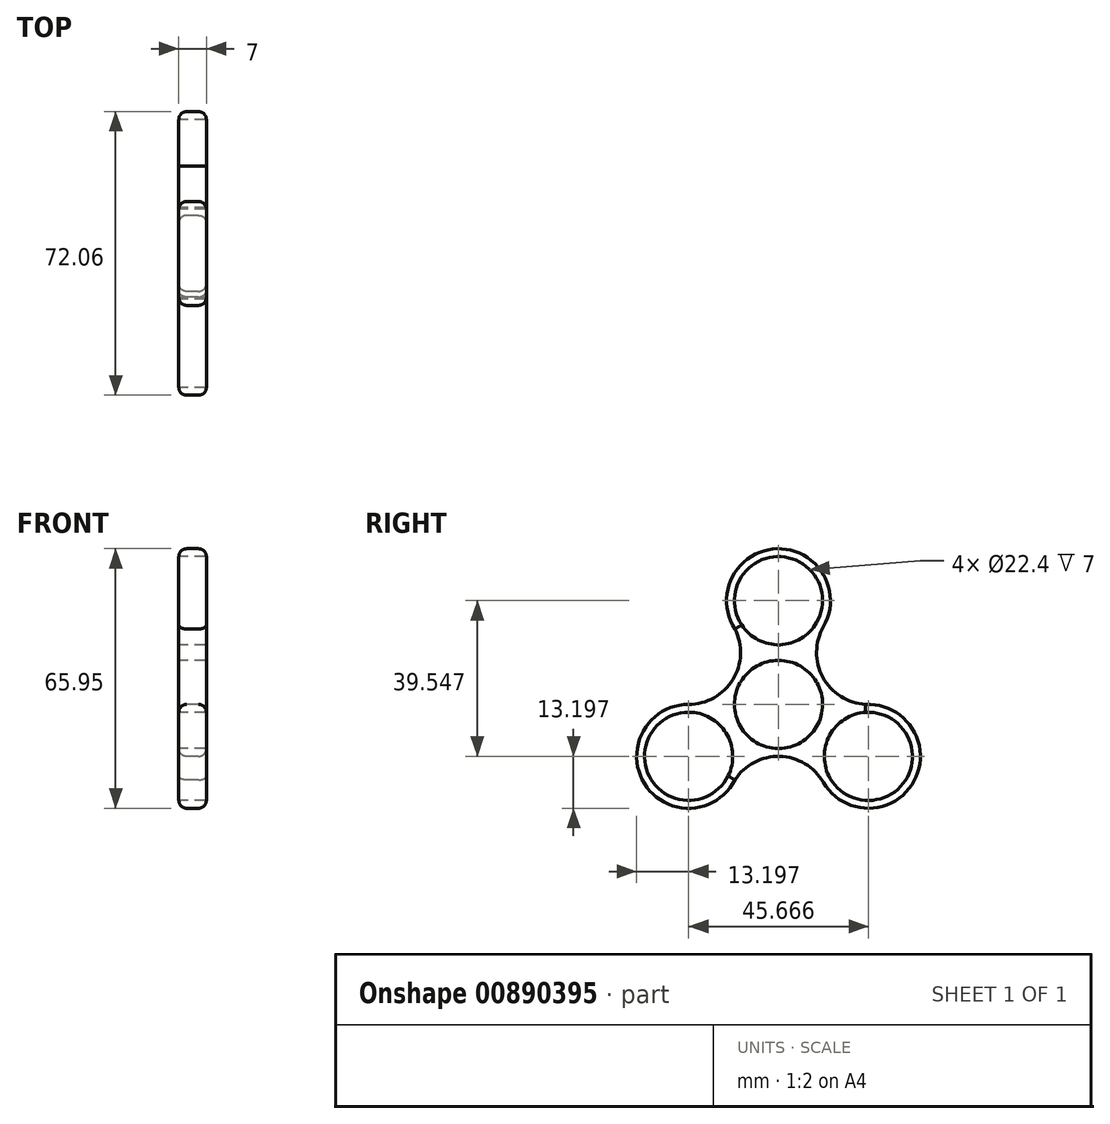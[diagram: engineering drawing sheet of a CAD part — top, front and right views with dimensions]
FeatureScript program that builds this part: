
annotation { "Feature Type Name" : "Feature", "Feature Type Description" : "" }
export const myFeature = defineFeature(function(context is Context, id is Id, definition is map)
    precondition{}
    {
        {
            var Q0;
            Q0=qCreatedBy(makeId("Right.planeOp"),FACE);
            var sketch = newSketch(context, id + "F0", { "sketchPlane" : qUnion([Q0])});
            skCircle(sketch, "E0", {"center": v(0, 0) * mm, "radius": 11.2 * mm});
            skArc(sketch, "E1", {"start": v(-11.34, 6.75) * mm, "mid": v(-11.43, 6.6) * mm, "end": v(-11.5, 6.47) * mm});
            skCircle(sketch, "E2", {"center": v(0, 26.37) * mm, "radius": 11.2 * mm});
            skArc(sketch, "E3.1.0", {"start": v(-22.84, 0.02) * mm, "mid": v(-34.09, -20.08) * mm, "end": v(-11.08, -19.19) * mm});
            skCircle(sketch, "E3.1.1", {"center": v(-22.83, -13.18) * mm, "radius": 11.2 * mm});
            skCircle(sketch, "E3.2.1", {"center": v(22.83, -13.18) * mm, "radius": 11.2 * mm});
            skArc(sketch, "E4", {"start": v(11.44, 19.77) * mm, "mid": v(11.27, 6.9) * mm, "end": v(22.15, 0) * mm});
            skArc(sketch, "E5.1.0", {"start": v(-22.84, 0.02) * mm, "mid": v(-11.6, 6.31) * mm, "end": v(-11.08, 19.19) * mm});
            skArc(sketch, "E5.2.0", {"start": v(11.4, -19.8) * mm, "mid": v(0.33, -13.2) * mm, "end": v(-11.08, -19.19) * mm});
            skArc(sketch, "E6.trimOffspring", {"start": v(11.44, 19.77) * mm, "mid": v(-0.34, 39.56) * mm, "end": v(-11.08, 19.19) * mm});
            skArc(sketch, "E7.trimOffspring", {"start": v(-0.18, -13.2) * mm, "mid": v(-0.01, -13.2) * mm, "end": v(0.15, -13.2) * mm});
            skArc(sketch, "E8.trimOffspring", {"start": v(11.52, 6.45) * mm, "mid": v(11.44, 6.6) * mm, "end": v(11.35, 6.73) * mm});
            skArc(sketch, "E9.trimOffspring", {"start": v(11.4, -19.8) * mm, "mid": v(34.43, -19.48) * mm, "end": v(22.15, 0) * mm});
            skSolve(sketch);
        }
        {
            var Q0;
            Q0=makeQuery(id+"F0.imprint","IMPRINT",FACE,{"disambiguationData":[TD([[makeQuery(id+"F0.imprint","IMPRINT",EDGE,{"derivedFrom":sQuery(id+"F0.wireOp",EDGE,"E0")}),-1.0]])]});
            extrude(context, id + "F1", {"entities" : qUnion([Q0]), "depth" : 7 * mm, "offsetDistance" : 25 * mm});
        }
        {
            var Q0;
            Q0=makeQuery(id+"F1.opExtrude","CAP_EDGE",EDGE,{"disambiguationData":[OSD([sQuery(id+"F0.wireOp",EDGE,"E5.1.0")])],"isStart":false});
            var Q1;
            Q1=makeQuery(id+"F1.opExtrude","CAP_EDGE",EDGE,{"disambiguationData":[OSD([sQuery(id+"F0.wireOp",EDGE,"E6.trimOffspring")])],"isStart":false});
            var Q2;
            Q2=makeQuery(id+"F1.opExtrude","CAP_EDGE",EDGE,{"disambiguationData":[OSD([sQuery(id+"F0.wireOp",EDGE,"E3.1.0")])],"isStart":false});
            var Q3;
            Q3=makeQuery(id+"F1.opExtrude","CAP_EDGE",EDGE,{"disambiguationData":[OSD([sQuery(id+"F0.wireOp",EDGE,"E5.2.0")])],"isStart":false});
            var Q4;
            Q4=makeQuery(id+"F1.opExtrude","CAP_EDGE",EDGE,{"disambiguationData":[OSD([sQuery(id+"F0.wireOp",EDGE,"E9.trimOffspring")])],"isStart":true});
            var Q5;
            Q5=makeQuery(id+"F1.opExtrude","CAP_EDGE",EDGE,{"disambiguationData":[OSD([sQuery(id+"F0.wireOp",EDGE,"E5.2.0")])],"isStart":true});
            var Q6;
            Q6=makeQuery(id+"F1.opExtrude","CAP_EDGE",EDGE,{"disambiguationData":[OSD([sQuery(id+"F0.wireOp",EDGE,"E3.1.0")])],"isStart":true});
            var Q7;
            Q7=makeQuery(id+"F1.opExtrude","CAP_EDGE",EDGE,{"disambiguationData":[OSD([sQuery(id+"F0.wireOp",EDGE,"E5.1.0")])],"isStart":true});
            var Q8;
            Q8=makeQuery(id+"F1.opExtrude","CAP_EDGE",EDGE,{"disambiguationData":[OSD([sQuery(id+"F0.wireOp",EDGE,"E6.trimOffspring")])],"isStart":true});
            fillet(context, id + "F2", {"entities" : qUnion([Q0, Q1, Q2, Q3, Q4, Q5, Q6, Q7, Q8]), "radius" : 2 * mm, "tangentPropagation" : true, "allowEdgeOverflow" : false});
        }
    });
